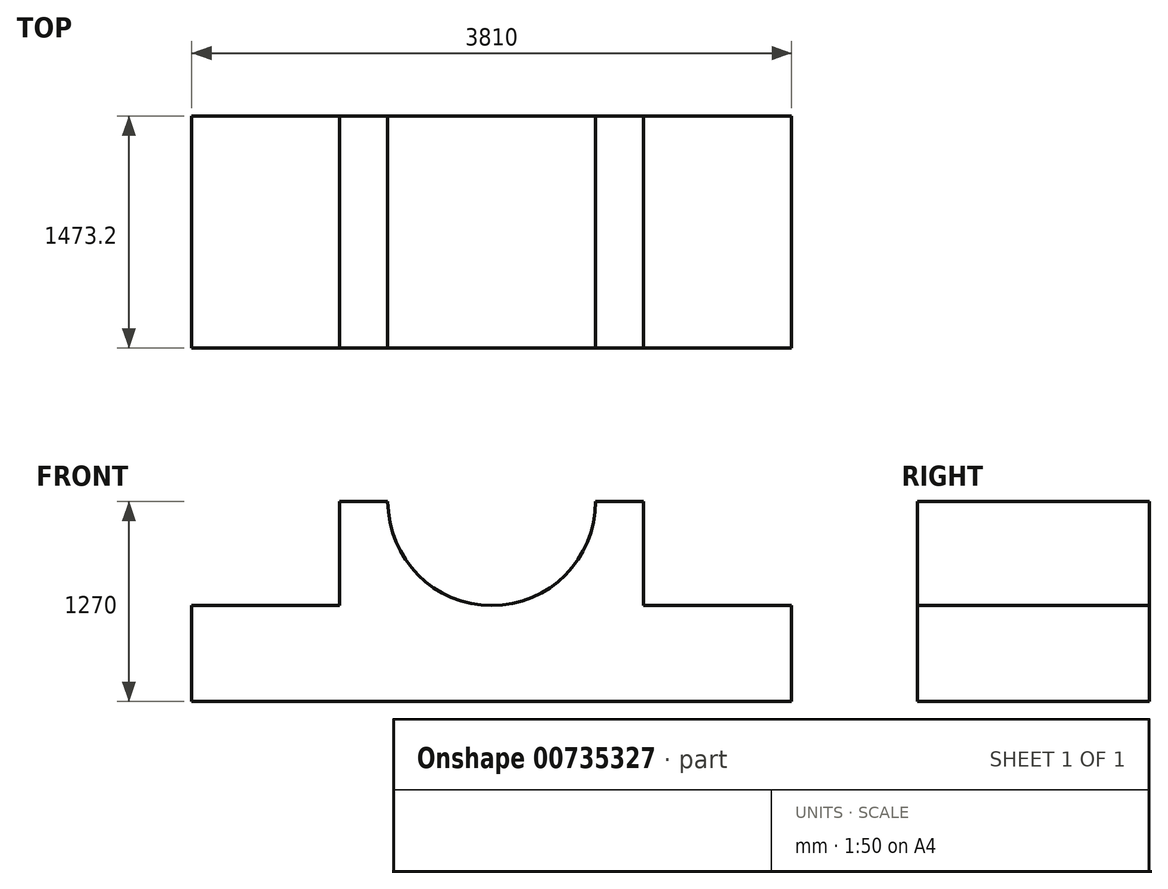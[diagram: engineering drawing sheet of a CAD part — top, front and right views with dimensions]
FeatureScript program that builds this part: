
annotation { "Feature Type Name" : "Feature", "Feature Type Description" : "" }
export const myFeature = defineFeature(function(context is Context, id is Id, definition is map)
    precondition{}
    {
        {
            var Q0;
            Q0=qCreatedBy(makeId("Front.planeOp"),FACE);
            var sketch = newSketch(context, id + "F0", { "sketchPlane" : qUnion([Q0])});
            skLineSegment(sketch, "E0", {"start": v(-75.51, 0) * mm, "end": v(3734.49, 0) * mm});
            skLineSegment(sketch, "E1", {"start": v(-75.51, 0) * mm, "end": v(-75.51, 609.6) * mm});
            skLineSegment(sketch, "E2", {"start": v(3734.49, 0) * mm, "end": v(3734.49, 609.6) * mm});
            skLineSegment(sketch, "E3", {"start": v(-75.51, 609.6) * mm, "end": v(864.29, 609.6) * mm});
            skLineSegment(sketch, "E4", {"start": v(864.29, 609.6) * mm, "end": v(864.29, 1270) * mm});
            skLineSegment(sketch, "E5", {"start": v(864.29, 1270) * mm, "end": v(1169.09, 1270) * mm});
            skLineSegment(sketch, "E6", {"start": v(3734.49, 609.6) * mm, "end": v(2794.69, 609.6) * mm});
            skLineSegment(sketch, "E7", {"start": v(2794.69, 609.6) * mm, "end": v(2794.69, 1270) * mm});
            skLineSegment(sketch, "E8", {"start": v(2794.69, 1270) * mm, "end": v(2489.89, 1270) * mm});
            skArc(sketch, "E9", {"start": v(1169.09, 1270) * mm, "mid": v(1829.49, 609.6) * mm, "end": v(2489.89, 1270) * mm});
            skSolve(sketch);
        }
        {
            var Q0;
            Q0=makeQuery(id+"F0.imprint","IMPRINT",FACE,{"disambiguationData":[TD([[makeQuery(id+"F0.imprint","IMPRINT",EDGE,{"derivedFrom":sQuery(id+"F0.wireOp",EDGE,"E0")}),1.0]])]});
            extrude(context, id + "F1", {"entities" : qUnion([Q0]), "depth" : 1473.2 * mm, "offsetDistance" : 25.4 * mm});
        }
    });
